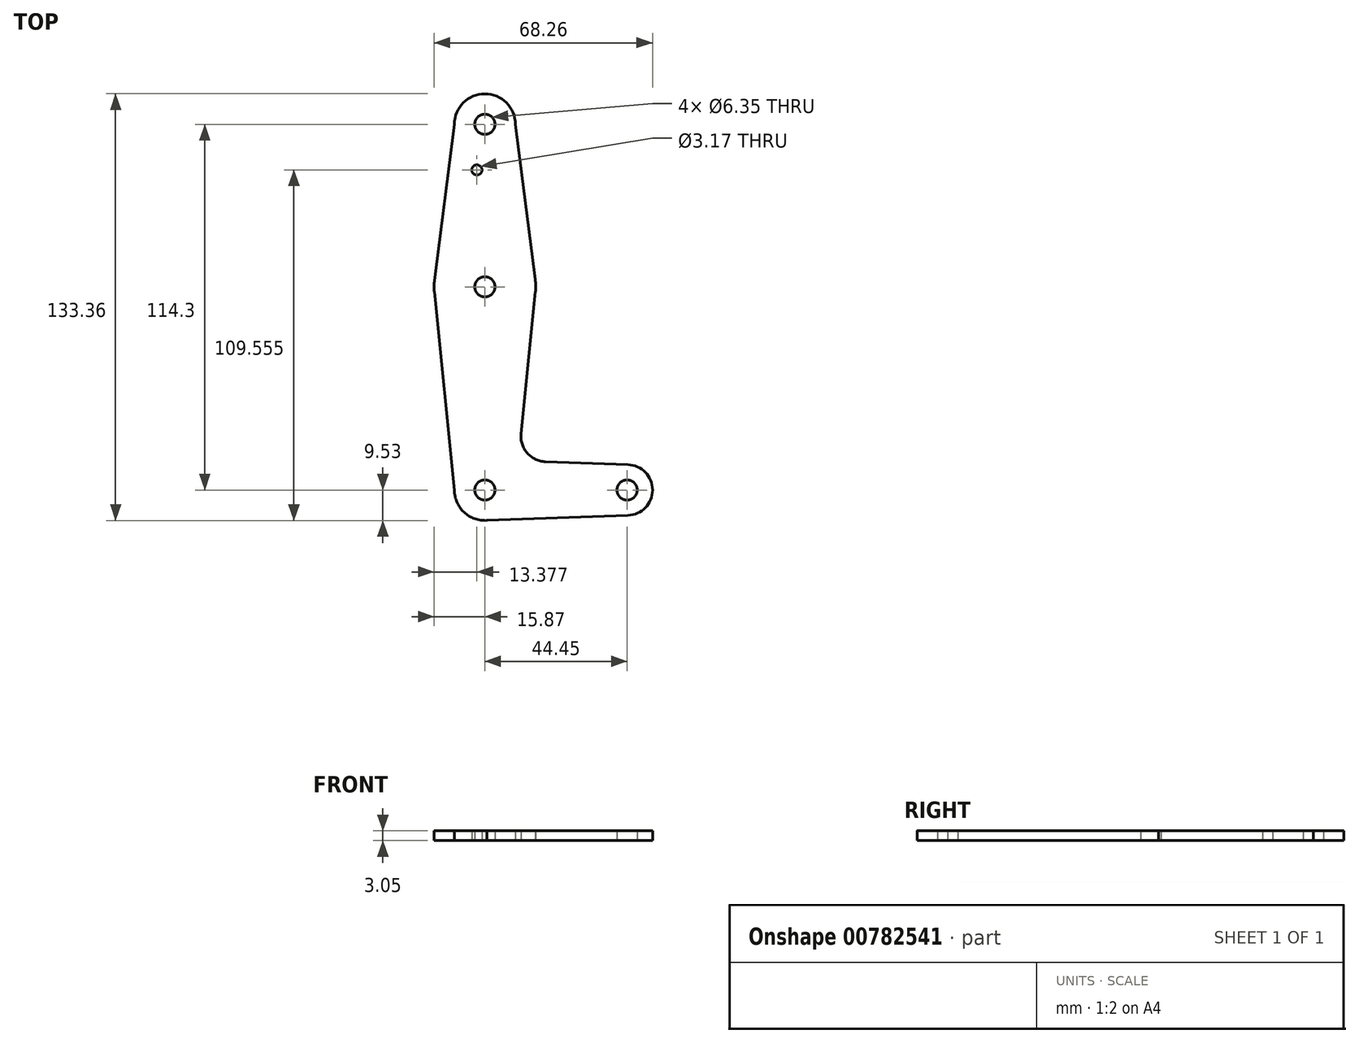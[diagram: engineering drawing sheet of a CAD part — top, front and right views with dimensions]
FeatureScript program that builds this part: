
annotation { "Feature Type Name" : "Feature", "Feature Type Description" : "" }
export const myFeature = defineFeature(function(context is Context, id is Id, definition is map)
    precondition{}
    {
        {
            var Q0;
            Q0=qCreatedBy(makeId("Top.planeOp"),FACE);
            var sketch = newSketch(context, id + "F0", { "sketchPlane" : qUnion([Q0])});
            skCircle(sketch, "E0", {"center": v(0, 0) * mm, "radius": 3.18 * mm});
            skCircle(sketch, "E1", {"center": v(0, 0) * mm, "radius": 9.53 * mm});
            skLineSegment(sketch, "E2", {"start": v(0, 0) * mm, "end": v(0, 63.5) * mm, "construction": true});
            skCircle(sketch, "E3", {"center": v(0, 63.5) * mm, "radius": 3.18 * mm});
            skCircle(sketch, "E4", {"center": v(0, 63.5) * mm, "radius": 15.88 * mm});
            skLineSegment(sketch, "E5", {"start": v(0, 0) * mm, "end": v(44.45, 0) * mm, "construction": true});
            skCircle(sketch, "E6", {"center": v(44.45, 0) * mm, "radius": 7.94 * mm});
            skLineSegment(sketch, "E7", {"start": v(0, 63.5) * mm, "end": v(0, 114.3) * mm, "construction": true});
            skCircle(sketch, "E8", {"center": v(0, 114.3) * mm, "radius": 9.53 * mm});
            skLineSegment(sketch, "E9", {"start": v(18.93, 8.85) * mm, "end": v(44.73, 7.93) * mm});
            skLineSegment(sketch, "E10", {"start": v(0, -9.53) * mm, "end": v(44.73, -7.93) * mm});
            skCircle(sketch, "E11", {"center": v(-2.5, 100.03) * mm, "radius": 1.59 * mm});
            skCircle(sketch, "E12", {"center": v(0, 114.3) * mm, "radius": 3.18 * mm});
            skLineSegment(sketch, "E13", {"start": v(-9.53, 0) * mm, "end": v(-15.8, 61.9) * mm});
            skLineSegment(sketch, "E14", {"start": v(11.3, 17.6) * mm, "end": v(15.8, 61.9) * mm});
            skLineSegment(sketch, "E15", {"start": v(-9.53, 114.3) * mm, "end": v(-15.75, 65.5) * mm});
            skLineSegment(sketch, "E16", {"start": v(9.53, 114.3) * mm, "end": v(15.8, 65.1) * mm});
            skPoint(sketch, "E17.newPointA", {"position": v(9.53, 0) * mm});
            skArc(sketch, "E17.filletArc", {"start": v(11.3, 17.6) * mm, "mid": v(13.22, 11.57) * mm, "end": v(18.93, 8.85) * mm});
            skCircle(sketch, "E18", {"center": v(44.45, 0) * mm, "radius": 3.18 * mm});
            skSolve(sketch);
        }
        {
            var Q0;
            Q0 = qSketchRegion(id + "F0", true);
            extrude(context, id + "F1", {"entities" : qUnion([Q0]), "depth" : 3.05 * mm, "offsetDistance" : 25.4 * mm});
        }
    });
